FCSTD DOCUMENT  (FreeCAD 2023.521R14555 (Git shallow))
Label: Y_asm
License: All rights reserved
objects: App::Link×6, App::DocumentObjectGroup×3, PartDesign::CoordinateSystem×1, App::FeaturePython×1, App::Part×1
note: 1 computed .brp shape members not serialized (recipe doc carries the construction recipe); baked Part::Feature solids carry a one-line shape summary decoded from their .brp
EXTERNAL_REF file=Y_8mm.FCStd obj=Local_CS
EXTERNAL_REF file=Y_Back_Base.FCStd obj=Local_CS
EXTERNAL_REF file=Y_8mm.FCStd obj=Part
EXTERNAL_REF file=Y_Back_Base.FCStd obj=Local_CS001
EXTERNAL_REF file=Y_8mm.FCStd obj=Local_CS001
EXTERNAL_REF file=Y_Back_Base.FCStd obj=Front_base
EXTERNAL_REF file=Y_Front_Base.FCStd obj=Local_CS001
EXTERNAL_REF file=Y_Front_Base.FCStd obj=Front_base
EXTERNAL_REF file=Y_Rod.FCStd obj=LCS_0
EXTERNAL_REF file=Y_Front_Base.FCStd obj=Local_CS003
EXTERNAL_REF file=Y_Rod.FCStd obj=Rod
EXTERNAL_REF file=Y_Front_Base.FCStd obj=Local_CS002

FEATURE [App::DocumentObjectGroup] Parts
  ClaimAllChildren = true
  ExportMode = 1
  TreeRank = 12
  _GroupVersion = 1
FEATURE [PartDesign::CoordinateSystem] LCS_Origin
  AttacherType = Attacher::AttachEngine3D
  AttachmentSupport = -> [X_Axis]
  InvalidShape = false
  MapMode = 2
  Support = -> [X_Axis]
  TreeRank = 4
  ValidateShape = false
FEATURE [App::DocumentObjectGroup] Constraints
  ClaimAllChildren = true
  ExportMode = 1
  TreeRank = 11
  _GroupVersion = 1
FEATURE [App::FeaturePython] Variables  # WARN: FeaturePython — macro-defined, semantics opaque (R4)
  TreeRank = 17
  Type = App::PropertyContainer
FEATURE [App::DocumentObjectGroup] Configurations
  ClaimAllChildren = true
  ExportMode = 1
  TreeRank = 18
  _GroupVersion = 1
FEATURE [App::Link] Y_Rod  label="Y_Rod(Y_Rod)"
  AttachedBy = #Local_CS
  AttachedTo = Front_base#Local_CS
  AutoLinkLabel = true
  AutoPlacement = true
  LinkPlacement = pos=(-90,-415,40) rot=(0,0,1;0rad)
  LinkedObject = -> <external Y_8mm.FCStd>#Part
  Placement = pos=(-90,-415,40) rot=(0,0,1;0rad)
  SolverId = Asm4EE
  SyncGroupVisibility = false
  TreeRank = 20
  _LinkVersion = 1
  expr: Placement = Front_base.Placement * Y_Back_Base#Local_CS.Placement * AttachmentOffset * Y_8mm#Local_CS.Placement ^ (-1)
FEATURE [App::Link] Y_Rod_Y_Rod_  label="Y_Rod(Y_Rod)001"
  AttachedBy = #Local_CS
  AttachedTo = Front_base#Local_CS001
  AutoLinkLabel = true
  AutoPlacement = true
  LinkPlacement = pos=(90,-415,40) rot=(0,0,1;0rad)
  LinkedObject = -> <external Y_8mm.FCStd>#Part
  Placement = pos=(90,-415,40) rot=(0,0,1;0rad)
  SolverId = Asm4EE
  SyncGroupVisibility = false
  TreeRank = 21
  _LinkVersion = 1
  expr: Placement = Front_base.Placement * Y_Back_Base#Local_CS001.Placement * AttachmentOffset * Y_8mm#Local_CS.Placement ^ (-1)
FEATURE [App::Link] Back_base  label="Back_base(Back_base)"
  AttachedBy = #Local_CS001
  AttachedTo = Y_Rod#Local_CS001
  AttachmentOffset = pos=(0,0,0) rot=(1,0,0;3.14159rad)
  AutoLinkLabel = true
  AutoPlacement = true
  LinkPlacement = pos=(2.84e-14,-830,1.99e-13) rot=(0,0,1;3.14159rad)
  LinkedObject = -> <external Y_Back_Base.FCStd>#Front_base
  Placement = pos=(2.84e-14,-830,1.99e-13) rot=(0,0,1;3.14159rad)
  SolverId = Asm4EE
  SyncGroupVisibility = false
  TreeRank = 22
  _LinkVersion = 1
  expr: Placement = Y_Rod.Placement * Y_8mm#Local_CS001.Placement * AttachmentOffset * Y_Back_Base#Local_CS001.Placement ^ (-1)
FEATURE [App::Link] Front_base  label="Front_base(Front_base)"
  AttachedBy = #Local_CS001
  AttachedTo = Y_Rod_Y_Rod_#Local_CS
  AutoLinkLabel = true
  AutoPlacement = true
  LinkPlacement = pos=(2.84e-14,-410,6.39e-14) rot=(0,0,1;0rad)
  LinkedObject = -> <external Y_Front_Base.FCStd>#Front_base
  Placement = pos=(2.84e-14,-410,6.39e-14) rot=(0,0,1;0rad)
  SolverId = Asm4EE
  SyncGroupVisibility = false
  TreeRank = 23
  _LinkVersion = 1
  expr: Placement = Y_Rod_Y_Rod_.Placement * Y_8mm#Local_CS.Placement * AttachmentOffset * Y_Front_Base#Local_CS001.Placement ^ (-1)
FEATURE [App::Link] Rod  label="Rod(Rod)"
  AttachedBy = #LCS_0
  AttachedTo = Front_base#Local_CS003
  AttachmentOffset = pos=(0,0,0) rot=(0,1,0;1.5708rad)
  AutoLinkLabel = true
  AutoPlacement = true
  LinkPlacement = pos=(-90,-424,20) rot=(-0.57735,0.57735,0.57735;4.18879rad)
  LinkedObject = -> <external Y_Rod.FCStd>#Rod
  Placement = pos=(-90,-424,20) rot=(-0.57735,0.57735,0.57735;4.18879rad)
  SolverId = Asm4EE
  SyncGroupVisibility = false
  TreeRank = 24
  _LinkVersion = 1
  expr: Placement = Front_base.Placement * Y_Front_Base#Local_CS003.Placement * AttachmentOffset * Unnamed1#LCS_0.Placement ^ (-1)
FEATURE [App::Link] Rod001  label="Rod"
  AttachedBy = #LCS_0
  AttachedTo = Front_base#Local_CS002
  AttachmentOffset = pos=(0,0,0) rot=(0,1,0;1.5708rad)
  AutoLinkLabel = true
  AutoPlacement = true
  LinkPlacement = pos=(90,-424,20) rot=(-0.57735,0.57735,0.57735;4.18879rad)
  LinkedObject = -> <external Y_Rod.FCStd>#Rod
  Placement = pos=(90,-424,20) rot=(-0.57735,0.57735,0.57735;4.18879rad)
  SolverId = Asm4EE
  SyncGroupVisibility = false
  TreeRank = 25
  _LinkVersion = 1
  expr: Placement = Front_base.Placement * Y_Front_Base#Local_CS002.Placement * AttachmentOffset * Unnamed1#LCS_0.Placement ^ (-1)
FEATURE [App::Part] Assembly
  AssemblyType = Part::Link
  ClaimAllChildren = false
  ExportMode = 1
  Group = -> [LCS_Origin,Constraints,Variables,Configurations,Y_Rod,Y_Rod_Y_Rod_,Back_base,Front_base,Rod,Rod001]
  Origin = -> Origin
  TreeRank = 14
  Type = Assembly
  _ExportChildren = -> [LCS_Origin,Constraints,Variables,Configurations,Y_Rod,Y_Rod_Y_Rod_,Back_base,Front_base,Rod,Rod001]
  _GroupVersion = 1

RESOLVED EXTERNAL PARTS (link-assembly join: the EXTERNAL_REF files above that resolve inside this repo's crawl, each included once):
---- part Y_8mm.FCStd = doc fcstd_2fb0b88b0bbf ----
FCSTD DOCUMENT  (FreeCAD 2023.521R14555 (Git shallow))
Label: Y_8mm
License: All rights reserved
objects: PartDesign::CoordinateSystem×2, Sketcher::SketchObject×1, PartDesign::Pad×1, PartDesign::Body×1, App::Part×1
note: 8 computed .brp shape members not serialized (recipe doc carries the construction recipe); baked Part::Feature solids carry a one-line shape summary decoded from their .brp

FEATURE [Sketcher::SketchObject] Sketch
  ArcFitTolerance = 1e-06
  AttachmentSupport = -> [XZ_Plane]
  ExternalBSplineMaxDegree = 5
  ExternalBSplineTolerance = 0.0001
  FullyConstrained = true
  InternalTolerance = 1e-06
  InvalidShape = false
  MakeInternals = false
  MapMode = 5
  Placement = pos=(0,0,0) rot=(1,0,0;1.5708rad)
  Support = -> [XZ_Plane]
  TreeRank = 14
  ValidateShape = false
  sketch-geometry (1):
    g0: Circle CenterX=0 CenterY=0 CenterZ=0 NormalX=0 NormalY=0 NormalZ=1 AngleXU=0 Radius=4
  constraints (2):
    c: Coincident(g0,g-1)
    c: Diameter(g0) = 8
FEATURE [PartDesign::Pad] Pad
  AddSubType = 0
  AlongSketchNormal = false
  AutoTaperInnerAngle = true
  CheckUpToFaceLimits = true
  ClaimChildren = false
  Direction = (0,-1,2e-16)
  Fit = 0
  FitJoin = 0
  InnerFit = 0
  InnerFitJoin = 0
  InvalidShape = false
  Length = 410
  Length2 = 10
  Linearize = true
  NewSolid = false
  Profile = -> Sketch
  ReferenceAxis = -> Sketch [N_Axis]
  Suppress = false
  TaperInnerAngle = 0
  TaperInnerAngleRev = 0
  TreeRank = 15
  Type = 0
  ValidateShape = true
  _ProfileBasedVersion = 1
FEATURE [PartDesign::Body] Body
  AutoGroupSolids = false
  ClaimAllChildren = false
  ExportMode = 0
  Group = -> [Sketch,Pad]
  InvalidShape = false
  Origin = -> Origin001
  Tip = -> Pad
  TreeRank = 13
  ValidateShape = false
  _ExportChildren = -> [Pad]
  _GroupVersion = 1
FEATURE [PartDesign::CoordinateSystem] Local_CS  label="Start"
  AttacherType = Attacher::AttachEngine3D
  AttachmentSupport = -> [Pad]
  InvalidShape = false
  MapMode = 11
  Placement = pos=(0,0,0) rot=(0.57735,-0.57735,0.57735;2.0944rad)
  Support = -> [Pad]
  TreeRank = 16
  ValidateShape = false
FEATURE [PartDesign::CoordinateSystem] Local_CS001  label="End"
  AttacherType = Attacher::AttachEngine3D
  AttachmentSupport = -> [Pad]
  InvalidShape = false
  MapMode = 11
  Placement = pos=(0,-410,9.1e-14) rot=(0.57735,-0.57735,0.57735;2.0944rad)
  Support = -> [Pad]
  TreeRank = 17
  ValidateShape = false
FEATURE [App::Part] Part  label="Y_Rod"
  ClaimAllChildren = false
  ExportMode = 1
  Group = -> [Body,Local_CS,Local_CS001]
  Origin = -> Origin
  TreeRank = 3
  _ExportChildren = -> [Body,Local_CS,Local_CS001]
  _GroupVersion = 1
---- part Y_Back_Base.FCStd = doc fcstd_6716cce88ba4 ----
FCSTD DOCUMENT  (FreeCAD 2023.521R14555 (Git shallow))
Label: Y_Back_Base
License: All rights reserved
objects: Sketcher::SketchObject×4, PartDesign::Pocket×3, PartDesign::CoordinateSystem×3, PartDesign::Pad×1, PartDesign::Fillet×1, PartDesign::Body×1, App::Part×1
note: 27 computed .brp shape members not serialized (recipe doc carries the construction recipe); baked Part::Feature solids carry a one-line shape summary decoded from their .brp

FEATURE [Sketcher::SketchObject] Sketch
  ArcFitTolerance = 1e-06
  AttachmentSupport = -> [XZ_Plane]
  ExternalBSplineMaxDegree = 5
  ExternalBSplineTolerance = 0.0001
  FullyConstrained = false
  InternalTolerance = 1e-06
  InvalidShape = false
  MakeInternals = false
  MapMode = 5
  Placement = pos=(0,0,0) rot=(1,0,0;1.5708rad)
  Support = -> [XZ_Plane]
  TreeRank = 11
  ValidateShape = false
  sketch-geometry (12):
    g0: Circle CenterX=-90 CenterY=20 CenterZ=0 NormalX=0 NormalY=0 NormalZ=1 AngleXU=0 Radius=4.25
    g1: Circle CenterX=90 CenterY=20 CenterZ=0 NormalX=0 NormalY=0 NormalZ=1 AngleXU=0 Radius=4.25
    g2: LineSegment StartX=-100 StartY=0 StartZ=0 EndX=-100 EndY=50 EndZ=0
    g3: LineSegment StartX=100 StartY=50 StartZ=0 EndX=100 EndY=0 EndZ=0
    g4: LineSegment StartX=100 StartY=0 StartZ=0 EndX=-100 EndY=0 EndZ=0
    g5: GeomPoint [constr] X=0 Y=25 Z=0
    g6: LineSegment StartX=-100 StartY=50 StartZ=0 EndX=-80 EndY=50 EndZ=0
    g7: LineSegment StartX=-80 StartY=50 StartZ=0 EndX=-80 EndY=15 EndZ=0
    g8: LineSegment StartX=-80 StartY=15 StartZ=0 EndX=80 EndY=15 EndZ=0
    g9: LineSegment StartX=80 StartY=15 StartZ=0 EndX=80 EndY=50 EndZ=0
    g10: LineSegment StartX=80 StartY=50 StartZ=0 EndX=100 EndY=50 EndZ=0
    g11: GeomPoint [constr] X=-90 Y=50 Z=0
  constraints (30):
    c: Coincident(g3,g4)
    c: Coincident(g4,g2)
    c: Horizontal(g4)
    c: Vertical(g2)
    c: Vertical(g3)
    c: Symmetric(g3,g2,g5)
    c: Symmetric(g1,g0,g-2)
    c: PointOnObject(g-1,g4)
    c: Vertical(g5,g-1)
    c: DistanceX(g0,g1) = 180
    c: DistanceX(g4,g4) = 200
    c: DistanceY(g-1,g0) = 20
    c: DistanceY(g2,g2) = 50
    c: Equal(g0,g1)
    c: Diameter(g0) = 8.5
    c: Coincident(g6,g2)
    c: Horizontal(g6)
    c: Vertical(g7)
    c: Coincident(g8,g7)
    c: Coincident(g9,g8)
    c: Vertical(g9)
    c: Coincident(g10,g9)
    c: Coincident(g10,g3)
    c: Horizontal(g10)
    c: Horizontal(g9,g6)
    c: Coincident(g6,g7)
    c: Symmetric(g7,g8,g-2)
    c: Vertical(g11,g0)
    c: DistanceY(g2,g7) = 15
    c: DistanceX(g8,g8) = 160
FEATURE [PartDesign::Pad] Pad
  AddSubType = 0
  AlongSketchNormal = false
  AutoTaperInnerAngle = true
  CheckUpToFaceLimits = false
  ClaimChildren = false
  Direction = (0,-1,2e-16)
  Fit = 0
  FitJoin = 0
  InnerFit = 0
  InnerFitJoin = 0
  InvalidShape = false
  Length = 20
  Length2 = 10
  Linearize = true
  NewSolid = false
  Profile = -> Sketch
  ReferenceAxis = -> Sketch [N_Axis]
  Suppress = false
  TaperInnerAngle = 0
  TaperInnerAngleRev = 0
  TreeRank = 12
  Type = 0
  ValidateShape = true
  _ProfileBasedVersion = 1
FEATURE [Sketcher::SketchObject] Sketch001
  ArcFitTolerance = 1e-06
  AttachmentSupport = -> [Pad]
  ExternalBSplineMaxDegree = 5
  ExternalBSplineTolerance = 0.0001
  ExternalGeometry = -> [Pad]
  FullyConstrained = true
  InternalTolerance = 1e-06
  InvalidShape = false
  MakeInternals = false
  MapMode = 5
  Placement = pos=(0,-20,4.4e-15) rot=(1,0,0;1.5708rad)
  Support = -> [Pad]
  TreeRank = 13
  ValidateShape = false
  sketch-geometry (2):
    g0: Circle CenterX=-90 CenterY=40 CenterZ=0 NormalX=0 NormalY=0 NormalZ=1 AngleXU=0 Radius=4
    g1: Circle CenterX=90 CenterY=40 CenterZ=0 NormalX=0 NormalY=0 NormalZ=1 AngleXU=0 Radius=4
  constraints (5):
    c: Equal(g1,g0)
    c: Vertical(g0,g-3)
    c: Diameter(g0) = 8
    c: Symmetric(g0,g1,g-2)
    c: DistanceY(g-1,g0) = 40
FEATURE [PartDesign::Pocket] Pocket
  AddSubType = 1
  AlongSketchNormal = false
  AutoTaperInnerAngle = true
  BaseFeature = -> Pad
  CheckUpToFaceLimits = true
  ClaimChildren = false
  Direction = (0,1,-2e-16)
  Fit = 0
  FitJoin = 0
  InnerFit = 0
  InnerFitJoin = 0
  InvalidShape = false
  Length = 0
  Length2 = 10
  Linearize = true
  NewSolid = false
  Offset = 5
  Profile = -> Sketch001
  ReferenceAxis = -> Sketch001 [N_Axis]
  Suppress = false
  TaperInnerAngle = 0
  TaperInnerAngleRev = 0
  TreeRank = 14
  Type = 3
  UpToFace = -> Pad [Face11]
  ValidateShape = true
  _ProfileBasedVersion = 1
  _Version = 1
FEATURE [Sketcher::SketchObject] Sketch003
  ArcFitTolerance = 1e-06
  AttachmentSupport = -> [XZ_Plane001]
  ExternalBSplineMaxDegree = 5
  ExternalBSplineTolerance = 0.0001
  FullyConstrained = true
  InternalTolerance = 1e-06
  InvalidShape = false
  MakeInternals = false
  MapMode = 2
  Placement = pos=(0,0,0) rot=(1,0,0;1.5708rad)
  Support = -> [XZ_Plane001]
  TreeRank = 17
  ValidateShape = false
  sketch-geometry (3):
    g0: Circle CenterX=0 CenterY=8 CenterZ=0 NormalX=0 NormalY=0 NormalZ=1 AngleXU=0 Radius=2.65
    g1: Circle CenterX=20 CenterY=8 CenterZ=0 NormalX=0 NormalY=0 NormalZ=1 AngleXU=0 Radius=2.65
    g2: Circle CenterX=-20 CenterY=8 CenterZ=0 NormalX=0 NormalY=0 NormalZ=1 AngleXU=0 Radius=2.65
  constraints (8):
    c: Symmetric(g1,g2,g0)
    c: Vertical(g0,g-1)
    c: Horizontal(g1,g0)
    c: DistanceX(g0,g1) = 20
    c: Diameter(g1) = 5.3
    c: Equal(g0,g2)
    c: Equal(g0,g1)
    c: DistanceY(g-1,g0) = 8
FEATURE [PartDesign::Pocket] Pocket002
  AddSubType = 1
  AlongSketchNormal = false
  AutoTaperInnerAngle = true
  BaseFeature = -> Pocket
  CheckUpToFaceLimits = true
  ClaimChildren = false
  Direction = (0,1,-2e-16)
  Fit = 0
  FitJoin = 0
  InnerFit = 0
  InnerFitJoin = 0
  InvalidShape = false
  Length = 13
  Length2 = 10
  Linearize = true
  NewSolid = false
  Profile = -> Sketch003
  ReferenceAxis = -> Sketch003 [N_Axis]
  Reversed = true
  Suppress = false
  TaperInnerAngle = 0
  TaperInnerAngleRev = 0
  TreeRank = 18
  Type = 0
  ValidateShape = true
  _ProfileBasedVersion = 1
  _Version = 1
FEATURE [PartDesign::Fillet] Fillet
  AddSubType = 0
  Base = -> Pocket002 [Edge2,Edge8,Edge32,Edge30]
  BaseFeature = -> Pocket002
  InvalidShape = false
  NewSolid = false
  Radius = 9
  SupportTransform = false
  Suppress = false
  TreeRank = 19
  UseAllEdges = false
  ValidateShape = true
FEATURE [PartDesign::CoordinateSystem] Local_CS  label="Rod0"
  AttacherType = Attacher::AttachEngine3D
  AttachmentSupport = -> [Fillet]
  InvalidShape = false
  MapMode = 11
  Placement = pos=(-90,-5,40) rot=(0.57735,-0.57735,0.57735;2.0944rad)
  Support = -> [Fillet]
  TreeRank = 20
  ValidateShape = false
FEATURE [PartDesign::CoordinateSystem] Local_CS001  label="Rod1"
  AttacherType = Attacher::AttachEngine3D
  AttachmentSupport = -> [Fillet]
  InvalidShape = false
  MapMode = 11
  Placement = pos=(90,-5,40) rot=(0.57735,-0.57735,0.57735;2.0944rad)
  Support = -> [Fillet]
  TreeRank = 21
  ValidateShape = false
FEATURE [PartDesign::CoordinateSystem] LCS_0
  AttacherType = Attacher::AttachEngine3D
  AttachmentSupport = -> [X_Axis001]
  InvalidShape = false
  MapMode = 2
  Support = -> [X_Axis001]
  TreeRank = 26
  ValidateShape = false
FEATURE [Sketcher::SketchObject] Sketch005
  ArcFitTolerance = 1e-06
  AttachmentSupport = -> [Fillet]
  ExternalBSplineMaxDegree = 5
  ExternalBSplineTolerance = 0.0001
  ExternalGeometry = -> [Fillet]
  FullyConstrained = true
  InternalTolerance = 1e-06
  InvalidShape = false
  MakeInternals = false
  MapMode = 5
  Placement = pos=(-100,0,0) rot=(0.57735,-0.57735,-0.57735;2.0944rad)
  Support = -> [Fillet]
  TreeRank = 36
  ValidateShape = false
  sketch-geometry (4):
    g0: Circle CenterX=5 CenterY=28 CenterZ=0 NormalX=0 NormalY=0 NormalZ=1 AngleXU=0 Radius=2.85
    g1: Circle CenterX=15 CenterY=28 CenterZ=0 NormalX=0 NormalY=0 NormalZ=1 AngleXU=0 Radius=2.85
    g2: GeomPoint [constr] X=10 Y=28 Z=0
    g3: GeomPoint [constr] X=10 Y=2.2e-15 Z=0
  constraints (8):
    c: DistanceY(g-1,g0) = 28
    c: Diameter(g0) = 5.7
    c: Equal(g0,g1)
    c: Symmetric(g-3,g-3,g3)
    c: Vertical(g3,g2)
    c: Symmetric(g0,g1,g2)
    c: Horizontal(g1,g0)
    c: DistanceX(g0,g1) = 10
FEATURE [PartDesign::Pocket] Pocket003
  AddSubType = 1
  AlongSketchNormal = false
  AutoTaperInnerAngle = true
  BaseFeature = -> Fillet
  CheckUpToFaceLimits = true
  ClaimChildren = false
  Direction = (1,0,0)
  Fit = 0
  FitJoin = 0
  InnerFit = 0
  InnerFitJoin = 0
  InvalidShape = false
  Length = 10
  Length2 = 10
  Linearize = true
  NewSolid = false
  Profile = -> Sketch005
  ReferenceAxis = -> Sketch005 [N_Axis]
  Suppress = false
  TaperInnerAngle = 0
  TaperInnerAngleRev = 0
  TreeRank = 37
  Type = 0
  ValidateShape = true
  _ProfileBasedVersion = 1
  _Version = 1
FEATURE [PartDesign::Body] Body  label="Front_Base"
  AutoGroupSolids = false
  ClaimAllChildren = false
  ExportMode = 0
  Group = -> [Sketch,Pad,Sketch001,Pocket,Sketch003,Pocket002,Fillet,Sketch005,Pocket003]
  InvalidShape = false
  Origin = -> Origin
  Tip = -> Pocket003
  TreeRank = 10
  ValidateShape = false
  _ExportChildren = -> [Pad,Pocket,Pocket002,Fillet,Pocket003]
  _GroupVersion = 1
FEATURE [App::Part] Front_base  label="Back_base"
  ClaimAllChildren = false
  ExportMode = 1
  Group = -> [LCS_0,Body,Local_CS,Local_CS001]
  Origin = -> Origin001
  TreeRank = 34
  _ExportChildren = -> [LCS_0,Body,Local_CS,Local_CS001]
  _GroupVersion = 1
---- part Y_Front_Base.FCStd = doc fcstd_426246c1c2f7 ----
FCSTD DOCUMENT  (FreeCAD 2023.521R14555 (Git shallow))
Label: Y_Front_Base
License: All rights reserved
objects: Part::SubShapeBinder×6, PartDesign::CoordinateSystem×5, Sketcher::SketchObject×4, PartDesign::Pocket×3, PartDesign::Pad×1, PartDesign::Fillet×1, PartDesign::Body×1, App::Part×1
note: 35 computed .brp shape members not serialized (recipe doc carries the construction recipe); baked Part::Feature solids carry a one-line shape summary decoded from their .brp

FEATURE [Sketcher::SketchObject] Sketch
  ArcFitTolerance = 1e-06
  AttachmentSupport = -> [XZ_Plane]
  ExternalBSplineMaxDegree = 5
  ExternalBSplineTolerance = 0.0001
  FullyConstrained = true
  InternalTolerance = 1e-06
  InvalidShape = false
  MakeInternals = false
  MapMode = 5
  Placement = pos=(0,0,0) rot=(1,0,0;1.5708rad)
  Support = -> [XZ_Plane]
  TreeRank = 11
  ValidateShape = false
  sketch-geometry (12):
    g0: Circle CenterX=-90 CenterY=20 CenterZ=0 NormalX=0 NormalY=0 NormalZ=1 AngleXU=0 Radius=4.25
    g1: Circle CenterX=90 CenterY=20 CenterZ=0 NormalX=0 NormalY=0 NormalZ=1 AngleXU=0 Radius=4.25
    g2: LineSegment StartX=-100 StartY=0 StartZ=0 EndX=-100 EndY=50 EndZ=0
    g3: LineSegment StartX=100 StartY=50 StartZ=0 EndX=100 EndY=0 EndZ=0
    g4: LineSegment StartX=100 StartY=0 StartZ=0 EndX=-100 EndY=0 EndZ=0
    g5: GeomPoint [constr] X=0 Y=25 Z=0
    g6: LineSegment StartX=-100 StartY=50 StartZ=0 EndX=-80 EndY=50 EndZ=0
    g7: LineSegment StartX=-80 StartY=50 StartZ=0 EndX=-80 EndY=15 EndZ=0
    g8: LineSegment StartX=-80 StartY=15 StartZ=0 EndX=80 EndY=15 EndZ=0
    g9: LineSegment StartX=80 StartY=15 StartZ=0 EndX=80 EndY=50 EndZ=0
    g10: LineSegment StartX=80 StartY=50 StartZ=0 EndX=100 EndY=50 EndZ=0
    g11: GeomPoint [constr] X=-90 Y=50 Z=0
  constraints (30):
    c: Coincident(g3,g4)
    c: Coincident(g4,g2)
    c: Horizontal(g4)
    c: Vertical(g2)
    c: Vertical(g3)
    c: Symmetric(g3,g2,g5)
    c: Symmetric(g1,g0,g-2)
    c: PointOnObject(g-1,g4)
    c: Vertical(g5,g-1)
    c: DistanceX(g0,g1) = 180
    c: DistanceX(g4,g4) = 200
    c: DistanceY(g-1,g0) = 20
    c: DistanceY(g2,g2) = 50
    c: Equal(g0,g1)
    c: Diameter(g0) = 8.5
    c: Coincident(g6,g2)
    c: Horizontal(g6)
    c: Vertical(g7)
    c: Coincident(g8,g7)
    c: Coincident(g9,g8)
    c: Vertical(g9)
    c: Coincident(g10,g9)
    c: Coincident(g10,g3)
    c: Horizontal(g10)
    c: Horizontal(g9,g6)
    c: Coincident(g6,g7)
    c: Symmetric(g7,g8,g-2)
    c: Symmetric(g2,g6,g11)
    c: Vertical(g11,g0)
    c: DistanceY(g2,g7) = 15
FEATURE [PartDesign::Pad] Pad
  AddSubType = 0
  AlongSketchNormal = false
  AutoTaperInnerAngle = true
  CheckUpToFaceLimits = true
  ClaimChildren = false
  Direction = (0,-1,2e-16)
  Fit = 0
  FitJoin = 0
  InnerFit = 0
  InnerFitJoin = 0
  InvalidShape = false
  Length = 20
  Length2 = 10
  Linearize = true
  NewSolid = false
  Profile = -> Sketch
  ReferenceAxis = -> Sketch [N_Axis]
  Suppress = false
  TaperInnerAngle = 0
  TaperInnerAngleRev = 0
  TreeRank = 12
  Type = 0
  ValidateShape = true
  _ProfileBasedVersion = 1
FEATURE [Sketcher::SketchObject] Sketch001
  ArcFitTolerance = 1e-06
  AttachmentSupport = -> [Pad]
  ExternalBSplineMaxDegree = 5
  ExternalBSplineTolerance = 0.0001
  ExternalGeometry = -> [Pad]
  FullyConstrained = true
  InternalTolerance = 1e-06
  InvalidShape = false
  MakeInternals = false
  MapMode = 5
  Placement = pos=(0,-20,4.4e-15) rot=(1,0,0;1.5708rad)
  Support = -> [Pad]
  TreeRank = 13
  ValidateShape = false
  sketch-geometry (2):
    g0: Circle CenterX=-90 CenterY=40 CenterZ=0 NormalX=0 NormalY=0 NormalZ=1 AngleXU=0 Radius=4
    g1: Circle CenterX=90 CenterY=40 CenterZ=0 NormalX=0 NormalY=0 NormalZ=1 AngleXU=0 Radius=4
  constraints (5):
    c: Equal(g1,g0)
    c: Vertical(g0,g-3)
    c: Diameter(g0) = 8
    c: Symmetric(g0,g1,g-2)
    c: DistanceY(g-1,g0) = 40
FEATURE [PartDesign::Pocket] Pocket
  AddSubType = 1
  AlongSketchNormal = false
  AutoTaperInnerAngle = true
  BaseFeature = -> Pad
  CheckUpToFaceLimits = true
  ClaimChildren = false
  Direction = (0,1,-2e-16)
  Fit = 0
  FitJoin = 0
  InnerFit = 0
  InnerFitJoin = 0
  InvalidShape = false
  Length = 0
  Length2 = 10
  Linearize = true
  NewSolid = false
  Offset = 5
  Profile = -> Sketch001
  ReferenceAxis = -> Sketch001 [N_Axis]
  Suppress = false
  TaperInnerAngle = 0
  TaperInnerAngleRev = 0
  TreeRank = 14
  Type = 3
  UpToFace = -> Pad [Face11]
  ValidateShape = true
  _ProfileBasedVersion = 1
  _Version = 1
FEATURE [Sketcher::SketchObject] Sketch002
  ArcFitTolerance = 1e-06
  AttachmentSupport = -> [Pocket]
  ExternalBSplineMaxDegree = 5
  ExternalBSplineTolerance = 0.0001
  ExternalGeometry = -> [Pocket]
  FullyConstrained = true
  InternalTolerance = 1e-06
  InvalidShape = false
  MakeInternals = false
  MapMode = 5
  Placement = pos=(0,0,0) rot=(0,0.707107,0.707107;3.14159rad)
  Support = -> [Pocket]
  TreeRank = 15
  ValidateShape = false
  sketch-geometry (14):
    g0: LineSegment StartX=-83 StartY=24.0415 StartZ=0 EndX=-90 EndY=28.0829 EndZ=0
    g1: LineSegment StartX=-90 StartY=28.0829 StartZ=0 EndX=-97 EndY=24.0415 EndZ=0
    g2: LineSegment StartX=-97 StartY=24.0415 StartZ=0 EndX=-97 EndY=15.9585 EndZ=0
    g3: LineSegment StartX=-97 StartY=15.9585 StartZ=0 EndX=-90 EndY=11.9171 EndZ=0
    g4: LineSegment StartX=-90 StartY=11.9171 StartZ=0 EndX=-83 EndY=15.9585 EndZ=0
    g5: LineSegment StartX=-83 StartY=15.9585 StartZ=0 EndX=-83 EndY=24.0415 EndZ=0
    g6: Circle [constr] CenterX=-90 CenterY=20 CenterZ=0 NormalX=0 NormalY=0 NormalZ=1 AngleXU=0 Radius=8.0829
    g7: LineSegment StartX=83 StartY=24.0415 StartZ=0 EndX=83 EndY=15.9585 EndZ=0
    g8: LineSegment StartX=83 StartY=15.9585 StartZ=0 EndX=90 EndY=11.9171 EndZ=0
    g9: LineSegment StartX=90 StartY=11.9171 StartZ=0 EndX=97 EndY=15.9585 EndZ=0
    g10: LineSegment StartX=97 StartY=15.9585 StartZ=0 EndX=97 EndY=24.0415 EndZ=0
    g11: LineSegment StartX=97 StartY=24.0415 StartZ=0 EndX=90 EndY=28.0829 EndZ=0
    g12: LineSegment StartX=90 StartY=28.0829 StartZ=0 EndX=83 EndY=24.0415 EndZ=0
    g13: Circle [constr] CenterX=90 CenterY=20 CenterZ=0 NormalX=0 NormalY=0 NormalZ=1 AngleXU=0 Radius=8.0829
  constraints (32):
    c: Coincident(g0,g1)
    c: Coincident(g1,g2)
    c: Coincident(g2,g3)
    c: Coincident(g3,g4)
    c: Coincident(g4,g5)
    c: Coincident(g5,g0)
    c: Equal(g0, g1-g5) x5
    c: PointOnObject(g0,g6)
    c: PointOnObject(g1,g6)
    c: PointOnObject(g2,g6)
    c: PointOnObject(g3,g6)
    c: PointOnObject(g4,g6)
    c: PointOnObject(g5,g6)
    c: Coincident(g6,g-3)
    c: Coincident(g7,g8)
    c: Coincident(g8,g9)
    c: Coincident(g9,g10)
    c: Coincident(g10,g11)
    c: Coincident(g11,g12)
    c: Coincident(g12,g7)
    c: Equal(g7, g8-g12) x5
    c: PointOnObject(g7,g13)
    c: PointOnObject(g8,g13)
    c: PointOnObject(g9,g13)
    c: PointOnObject(g10,g13)
    c: PointOnObject(g11,g13)
    c: PointOnObject(g12,g13)
    c: Symmetric(g-3,g13,g-2)
    c: Equal(g5,g10)
    c: DistanceX(g1,g0) = 14
    c: Vertical(g5)
    c: Vertical(g10)
FEATURE [PartDesign::Pocket] Pocket001
  AddSubType = 1
  AlongSketchNormal = false
  AutoTaperInnerAngle = true
  BaseFeature = -> Pocket
  CheckUpToFaceLimits = true
  ClaimChildren = false
  Direction = (0,-1,2e-16)
  Fit = 0
  FitJoin = 0
  InnerFit = 0
  InnerFitJoin = 0
  InvalidShape = false
  Length = 14
  Length2 = 10
  Linearize = true
  NewSolid = false
  Profile = -> Sketch002
  ReferenceAxis = -> Sketch002 [N_Axis]
  Suppress = false
  TaperInnerAngle = 0
  TaperInnerAngleRev = 0
  TreeRank = 16
  Type = 0
  ValidateShape = true
  _ProfileBasedVersion = 1
  _Version = 1
FEATURE [Sketcher::SketchObject] Sketch003
  ArcFitTolerance = 1e-06
  AttachmentSupport = -> [Pocket001]
  ExternalBSplineMaxDegree = 5
  ExternalBSplineTolerance = 0.0001
  FullyConstrained = true
  InternalTolerance = 1e-06
  InvalidShape = false
  MakeInternals = false
  MapMode = 5
  Placement = pos=(0,0,0) rot=(0,0.707107,0.707107;3.14159rad)
  Support = -> [Pocket001]
  TreeRank = 17
  ValidateShape = false
  sketch-geometry (3):
    g0: Circle CenterX=0 CenterY=8 CenterZ=0 NormalX=0 NormalY=0 NormalZ=1 AngleXU=0 Radius=2.65
    g1: Circle CenterX=20 CenterY=8 CenterZ=0 NormalX=0 NormalY=0 NormalZ=1 AngleXU=0 Radius=2.65
    g2: Circle CenterX=-20 CenterY=8 CenterZ=0 NormalX=0 NormalY=0 NormalZ=1 AngleXU=0 Radius=2.65
  constraints (8):
    c: Symmetric(g1,g2,g0)
    c: Vertical(g0,g-1)
    c: Horizontal(g1,g0)
    c: DistanceX(g0,g1) = 20
    c: Diameter(g1) = 5.3
    c: Equal(g0,g2)
    c: Equal(g0,g1)
    c: DistanceY(g-1,g0) = 8
FEATURE [PartDesign::Pocket] Pocket002
  AddSubType = 1
  AlongSketchNormal = false
  AutoTaperInnerAngle = true
  BaseFeature = -> Pocket001
  CheckUpToFaceLimits = true
  ClaimChildren = false
  Direction = (0,-1,2e-16)
  Fit = 0
  FitJoin = 0
  InnerFit = 0
  InnerFitJoin = 0
  InvalidShape = false
  Length = 13
  Length2 = 10
  Linearize = true
  NewSolid = false
  Profile = -> Sketch003
  ReferenceAxis = -> Sketch003 [N_Axis]
  Suppress = false
  TaperInnerAngle = 0
  TaperInnerAngleRev = 0
  TreeRank = 18
  Type = 0
  ValidateShape = true
  _ProfileBasedVersion = 1
  _Version = 1
FEATURE [PartDesign::Fillet] Fillet
  AddSubType = 0
  Base = -> Pocket002 [Edge2,Edge8,Edge42,Edge40]
  BaseFeature = -> Pocket002
  InvalidShape = false
  NewSolid = false
  Radius = 9
  SupportTransform = false
  Suppress = false
  TreeRank = 19
  UseAllEdges = false
  ValidateShape = true
FEATURE [PartDesign::Body] Body  label="Front_Base"
  AutoGroupSolids = false
  ClaimAllChildren = false
  ExportMode = 0
  Group = -> [Sketch,Pad,Sketch001,Pocket,Sketch002,Pocket001,Sketch003,Pocket002,Fillet]
  InvalidShape = false
  Origin = -> Origin
  Tip = -> Fillet
  TreeRank = 10
  ValidateShape = false
  _ExportChildren = -> [Pad,Pocket,Pocket001,Pocket002,Fillet]
  _GroupVersion = 1
FEATURE [PartDesign::CoordinateSystem] Local_CS  label="Rod0"
  AttacherType = Attacher::AttachEngine3D
  AttachmentSupport = -> [Fillet]
  InvalidShape = false
  MapMode = 11
  Placement = pos=(-90,-5,40) rot=(0.57735,-0.57735,0.57735;2.0944rad)
  Support = -> [Fillet]
  TreeRank = 20
  ValidateShape = false
FEATURE [PartDesign::CoordinateSystem] Local_CS001  label="Rod1"
  AttacherType = Attacher::AttachEngine3D
  AttachmentSupport = -> [Fillet]
  InvalidShape = false
  MapMode = 11
  Placement = pos=(90,-5,40) rot=(0.57735,-0.57735,0.57735;2.0944rad)
  Support = -> [Fillet]
  TreeRank = 21
  ValidateShape = false
FEATURE [PartDesign::CoordinateSystem] Local_CS002  label="TRod0"
  AttacherType = Attacher::AttachEngine3D
  AttachmentSupport = -> [Fillet]
  InvalidShape = false
  MapMode = 45
  Placement = pos=(90,-14,20) rot=(0,0.707107,0.707107;3.14159rad)
  Support = -> [Fillet]
  TreeRank = 22
  ValidateShape = false
FEATURE [PartDesign::CoordinateSystem] Local_CS003  label="TRod1"
  AttacherType = Attacher::AttachEngine3D
  AttachmentSupport = -> [Fillet]
  InvalidShape = false
  MapMode = 45
  Placement = pos=(-90,-14,20) rot=(0,0.707107,0.707107;3.14159rad)
  Support = -> [Fillet]
  TreeRank = 23
  ValidateShape = false
FEATURE [PartDesign::CoordinateSystem] LCS_0
  AttacherType = Attacher::AttachEngine3D
  AttachmentSupport = -> [X_Axis001]
  InvalidShape = false
  MapMode = 2
  Support = -> [X_Axis001]
  TreeRank = 26
  ValidateShape = false
FEATURE [Part::SubShapeBinder] Binder  label="Binder(Fillet)"
  BindCopyOnChange = 0
  BindMode = 0
  ClaimChildren = false
  Context = -> Front_base [Binder.]
  EdgeTolerance = 1e-06
  FillStyle = 0
  Fuse = false
  InvalidShape = false
  MakeFace = true
  MergeEdges = true
  OffsetFill = false
  OffsetIntersection = false
  OffsetJoinType = 0
  OffsetOpenResult = false
  Outline = false
  PartialLoad = false
  Relative = true
  SplitEdges = false
  Support = -> [Body[Fillet.]]
  TightBound = false
  TreeRank = 35
  ValidateShape = false
  _Version = 8
FEATURE [Part::SubShapeBinder] Binder001  label="Binder001(Fillet)"
  BindCopyOnChange = 0
  BindMode = 0
  ClaimChildren = false
  Context = -> Front_base [Binder001.]
  EdgeTolerance = 1e-06
  FillStyle = 0
  Fuse = false
  InvalidShape = false
  MakeFace = true
  MergeEdges = true
  OffsetFill = false
  OffsetIntersection = false
  OffsetJoinType = 0
  OffsetOpenResult = false
  Outline = false
  PartialLoad = false
  Relative = true
  SplitEdges = false
  Support = -> [Body[Fillet.]]
  TightBound = false
  TreeRank = 36
  ValidateShape = false
  _Version = 8
FEATURE [Part::SubShapeBinder] Binder002  label="Binder002(Fillet)"
  BindCopyOnChange = 0
  BindMode = 0
  ClaimChildren = false
  Context = -> Front_base [Binder002.]
  EdgeTolerance = 1e-06
  FillStyle = 0
  Fuse = false
  InvalidShape = false
  MakeFace = true
  MergeEdges = true
  OffsetFill = false
  OffsetIntersection = false
  OffsetJoinType = 0
  OffsetOpenResult = false
  Outline = false
  PartialLoad = false
  Relative = true
  SplitEdges = false
  Support = -> [Body[Fillet.]]
  TightBound = false
  TreeRank = 37
  ValidateShape = false
  _Version = 8
FEATURE [Part::SubShapeBinder] Binder003  label="Binder003(Fillet)"
  BindCopyOnChange = 0
  BindMode = 0
  ClaimChildren = false
  Context = -> Front_base [Binder003.]
  EdgeTolerance = 1e-06
  FillStyle = 0
  Fuse = false
  InvalidShape = false
  MakeFace = true
  MergeEdges = true
  OffsetFill = false
  OffsetIntersection = false
  OffsetJoinType = 0
  OffsetOpenResult = false
  Outline = false
  PartialLoad = false
  Relative = true
  SplitEdges = false
  Support = -> [Body[Fillet.]]
  TightBound = false
  TreeRank = 38
  ValidateShape = false
  _Version = 8
FEATURE [Part::SubShapeBinder] Binder004  label="Binder004(Fillet)"
  BindCopyOnChange = 0
  BindMode = 0
  ClaimChildren = false
  Context = -> Front_base [Binder004.]
  EdgeTolerance = 1e-06
  FillStyle = 0
  Fuse = false
  InvalidShape = false
  MakeFace = true
  MergeEdges = true
  OffsetFill = false
  OffsetIntersection = false
  OffsetJoinType = 0
  OffsetOpenResult = false
  Outline = false
  PartialLoad = false
  Relative = true
  SplitEdges = false
  Support = -> [Body[Fillet.]]
  TightBound = false
  TreeRank = 39
  ValidateShape = false
  _Version = 8
FEATURE [Part::SubShapeBinder] Binder005  label="Binder005(Fillet)"
  BindCopyOnChange = 0
  BindMode = 0
  ClaimChildren = false
  Context = -> Front_base [Binder005.]
  EdgeTolerance = 1e-06
  FillStyle = 0
  Fuse = false
  InvalidShape = false
  MakeFace = true
  MergeEdges = true
  OffsetFill = false
  OffsetIntersection = false
  OffsetJoinType = 0
  OffsetOpenResult = false
  Outline = false
  PartialLoad = false
  Relative = true
  SplitEdges = false
  Support = -> [Body[Fillet.]]
  TightBound = false
  TreeRank = 40
  ValidateShape = false
  _Version = 8
FEATURE [App::Part] Front_base
  ClaimAllChildren = false
  ExportMode = 1
  Group = -> [LCS_0,Body,Local_CS,Local_CS001,Local_CS002,Local_CS003,Binder,Binder001,Binder002,Binder003,Binder004,Binder005]
  Origin = -> Origin001
  TreeRank = 34
  _ExportChildren = -> [LCS_0,Body,Local_CS,Local_CS001,Local_CS002,Local_CS003,Binder,Binder001,Binder002,Binder003,Binder004,Binder005]
  _GroupVersion = 1
---- part Y_Rod.FCStd = doc fcstd_640872c7d5d9 ----
FCSTD DOCUMENT  (FreeCAD 2023.521R14555 (Git shallow))
Label: Y_Rod
License: All rights reserved
objects: PartDesign::CoordinateSystem×3, Sketcher::SketchObject×2, PartDesign::Pad×2, PartDesign::Body×1, App::Part×1
note: 14 computed .brp shape members not serialized (recipe doc carries the construction recipe); baked Part::Feature solids carry a one-line shape summary decoded from their .brp

FEATURE [PartDesign::CoordinateSystem] LCS_0
  AttacherType = Attacher::AttachEngine3D
  AttachmentSupport = -> [X_Axis]
  InvalidShape = false
  MapMode = 2
  Support = -> [X_Axis]
  TreeRank = 3
  ValidateShape = false
FEATURE [PartDesign::CoordinateSystem] LCS_0001
  AttacherType = Attacher::AttachEngine3D
  AttachmentSupport = -> [X_Axis001]
  InvalidShape = false
  MapMode = 2
  Support = -> [X_Axis001]
  TreeRank = 21
  ValidateShape = false
FEATURE [Sketcher::SketchObject] Sketch
  ArcFitTolerance = 1e-06
  AttachmentSupport = -> [YZ_Plane001]
  ExternalBSplineMaxDegree = 5
  ExternalBSplineTolerance = 0.0001
  FullyConstrained = true
  InternalTolerance = 1e-06
  InvalidShape = false
  MakeInternals = false
  MapMode = 5
  Placement = pos=(0,0,0) rot=(0.57735,0.57735,0.57735;2.0944rad)
  Support = -> [YZ_Plane001]
  TreeRank = 23
  ValidateShape = false
  sketch-geometry (1):
    g0: Circle CenterX=0 CenterY=0 CenterZ=0 NormalX=0 NormalY=0 NormalZ=1 AngleXU=0 Radius=4
  constraints (2):
    c: Coincident(g0,g-1)
    c: Diameter(g0) = 8
FEATURE [PartDesign::Pad] Pad
  AddSubType = 0
  AlongSketchNormal = false
  AutoTaperInnerAngle = true
  CheckUpToFaceLimits = true
  ClaimChildren = false
  Direction = (1,-2e-16,3e-16)
  Fit = 0
  FitJoin = 0
  InnerFit = 0
  InnerFitJoin = 0
  InvalidShape = false
  Length = 420
  Length2 = 10
  Linearize = true
  NewSolid = false
  Profile = -> Sketch
  ReferenceAxis = -> Sketch [N_Axis]
  Suppress = false
  TaperInnerAngle = 0
  TaperInnerAngleRev = 0
  TreeRank = 24
  Type = 0
  ValidateShape = true
  _ProfileBasedVersion = 1
FEATURE [Sketcher::SketchObject] Sketch001
  ArcFitTolerance = 1e-06
  AttachmentSupport = -> [Pad]
  ExternalBSplineMaxDegree = 5
  ExternalBSplineTolerance = 0.0001
  FullyConstrained = true
  InternalTolerance = 1e-06
  InvalidShape = false
  MakeInternals = false
  MapMode = 5
  Placement = pos=(0,0,0) rot=(-0.57735,0.57735,0.57735;4.18879rad)
  Support = -> [Pad]
  TreeRank = 25
  ValidateShape = false
  sketch-geometry (7):
    g0: LineSegment StartX=7 StartY=4.04145 StartZ=0 EndX=-1.8e-15 EndY=8.0829 EndZ=0
    g1: LineSegment StartX=-1.5e-15 StartY=8.0829 StartZ=0 EndX=-7 EndY=4.04145 EndZ=0
    g2: LineSegment StartX=-7 StartY=4.04145 StartZ=0 EndX=-7 EndY=-4.04145 EndZ=0
    g3: LineSegment StartX=-7 StartY=-4.04145 StartZ=0 EndX=9e-16 EndY=-8.0829 EndZ=0
    g4: LineSegment StartX=5e-16 StartY=-8.0829 StartZ=0 EndX=7 EndY=-4.04145 EndZ=0
    g5: LineSegment StartX=7 StartY=-4.04145 StartZ=0 EndX=7 EndY=4.04145 EndZ=0
    g6: Circle [constr] CenterX=0 CenterY=0 CenterZ=0 NormalX=0 NormalY=0 NormalZ=1 AngleXU=0 Radius=8.0829
  constraints (16):
    c: Coincident(g0,g1)
    c: Coincident(g1,g2)
    c: Coincident(g2,g3)
    c: Coincident(g3,g4)
    c: Coincident(g4,g5)
    c: Coincident(g5,g0)
    c: Equal(g0, g1-g5) x5
    c: PointOnObject(g0,g6)
    c: PointOnObject(g1,g6)
    c: PointOnObject(g2,g6)
    c: PointOnObject(g3,g6)
    c: PointOnObject(g4,g6)
    c: PointOnObject(g5,g6)
    c: Coincident(g6,g-1)
    c: DistanceX(g1,g0) = 14
    c: Vertical(g2)
FEATURE [PartDesign::Pad] Pad001
  AddSubType = 0
  AlongSketchNormal = false
  AutoTaperInnerAngle = true
  BaseFeature = -> Pad
  CheckUpToFaceLimits = true
  ClaimChildren = false
  Direction = (-1,2e-16,-2e-16)
  Fit = 0
  FitJoin = 0
  InnerFit = 0
  InnerFitJoin = 0
  InvalidShape = false
  Length = 12
  Length2 = 10
  Linearize = true
  NewSolid = false
  Profile = -> Sketch001
  ReferenceAxis = -> Sketch001 [N_Axis]
  Suppress = false
  TaperInnerAngle = 0
  TaperInnerAngleRev = 0
  TreeRank = 26
  Type = 0
  ValidateShape = true
  _ProfileBasedVersion = 1
FEATURE [PartDesign::CoordinateSystem] Local_CS
  AttacherType = Attacher::AttachEngine3D
  AttachmentSupport = -> [Pad001]
  InvalidShape = false
  MapMode = 5
  Placement = pos=(-12,2.7e-15,-2.7e-15) rot=(-0.57735,0.57735,0.57735;4.18879rad)
  Support = -> [Pad001]
  TreeRank = 27
  ValidateShape = false
FEATURE [PartDesign::Body] Body
  AutoGroupSolids = false
  ClaimAllChildren = false
  ExportMode = 0
  Group = -> [LCS_0001,Sketch,Pad,Sketch001,Pad001,Local_CS]
  InvalidShape = false
  Origin = -> Origin001
  Tip = -> Pad001
  TreeRank = 22
  ValidateShape = false
  _ExportChildren = -> [LCS_0001,Pad,Pad001,Local_CS]
  _GroupVersion = 1
FEATURE [App::Part] Rod
  ClaimAllChildren = false
  ExportMode = 1
  Group = -> [LCS_0,Body]
  Origin = -> Origin
  TreeRank = 11
  _ExportChildren = -> [LCS_0,Body]
  _GroupVersion = 1
